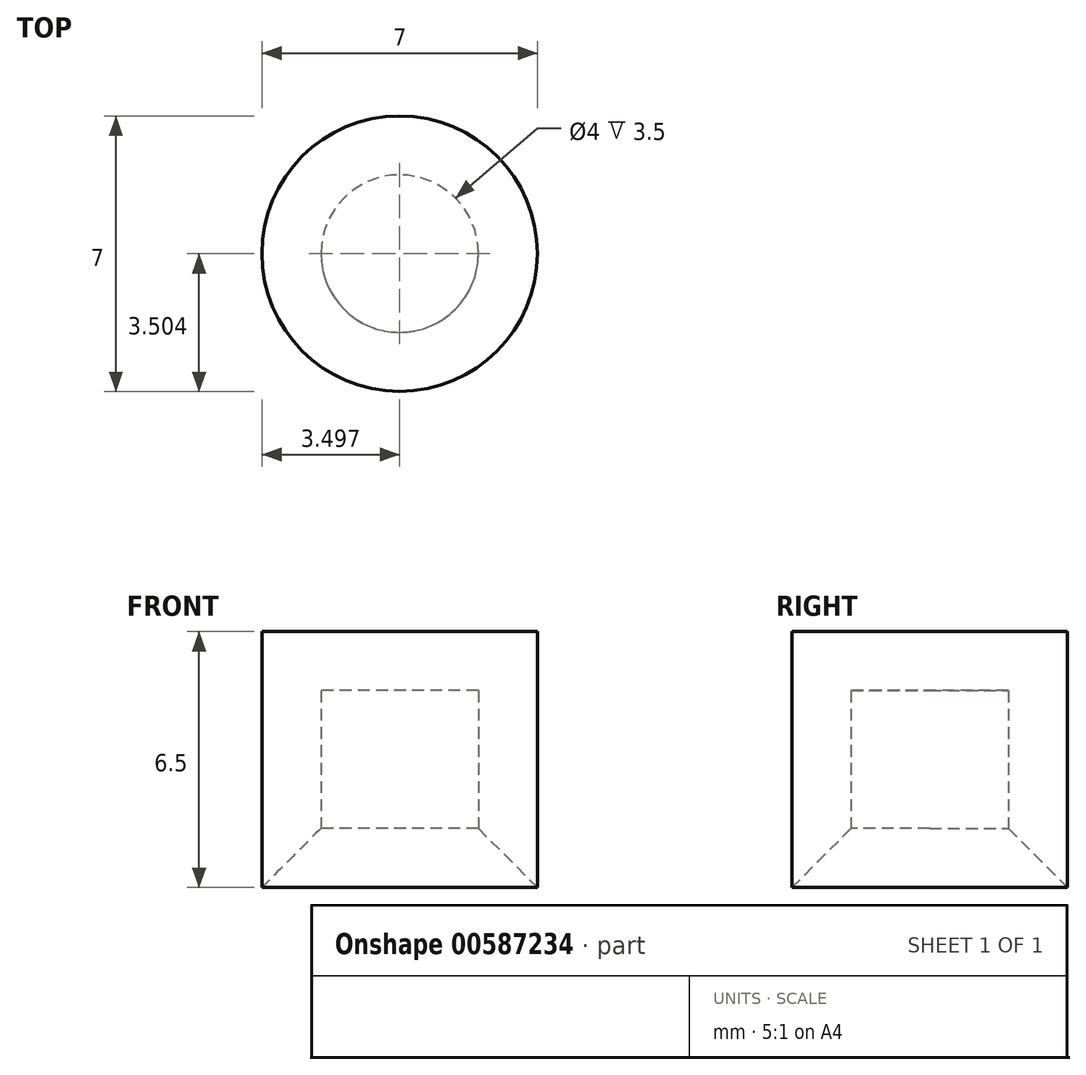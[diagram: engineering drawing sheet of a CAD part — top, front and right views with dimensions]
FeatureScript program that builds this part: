
annotation { "Feature Type Name" : "Feature", "Feature Type Description" : "" }
export const myFeature = defineFeature(function(context is Context, id is Id, definition is map)
    precondition{}
    {
        {
            var Q0;
            Q0=qCreatedBy(makeId("Top.planeOp"),FACE);
            var sketch = newSketch(context, id + "F0", { "sketchPlane" : qUnion([Q0])});
            skCircle(sketch, "E0", {"center": v(-2.51, -2.44) * mm, "radius": 3.5 * mm});
            skSolve(sketch);
        }
        {
            var Q0;
            Q0=makeQuery(id+"F0.imprint","IMPRINT",FACE,{"disambiguationData":[TD([[makeQuery(id+"F0.imprint","IMPRINT",EDGE,{"derivedFrom":sQuery(id+"F0.wireOp",EDGE,"E0")}),1.0]])]});
            extrude(context, id + "F1", {"entities" : qUnion([Q0]), "depth" : 10 * mm, "offsetDistance" : 25 * mm});
        }
        {
            var Q0;
            Q0=makeQuery(id+"F1.opExtrude","CAP_FACE",FACE,{"disambiguationData":[OSD([sQuery(id+"F0.wireOp",EDGE,"E0")])],"isStart":true});
            shell(context, id + "F2", {"entities" : qUnion([Q0]), "thickness" : 1.5 * mm});
        }
        {
            var Q0;
            {var subQ0=sQuery(id+"F0.wireOp",EDGE,"E0");Q0=makeQuery(id+"F2.opShell","OFFSET_EDGE",EDGE,{"disambiguationData":[OSD([subQ0]),TDD([makeQuery(id+"F1.opExtrude","CAP_EDGE",EDGE,{"disambiguationData":[OSD([subQ0])],"isStart":true})])]});}
            chamfer(context, id + "F3", {"entities" : qUnion([Q0]), "width" : 5 * mm, "tangentPropagation" : true});
        }
    });
